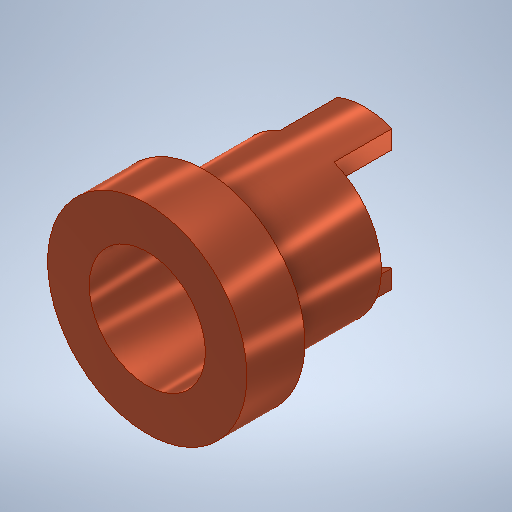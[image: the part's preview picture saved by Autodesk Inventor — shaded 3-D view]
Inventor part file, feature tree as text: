
AUTODESK INVENTOR PART (.ipt)
format: ipt  version: 2025.2 (Build 292293000, 293)  size: 283,648 bytes
history: native  units: mm
features: extrude x4, sketch x4, other x3, projected_geometry x2
ambient origin geometry x8: Origin, YZ Plane, XZ Plane, XY Plane, X Axis, Y Axis, Z Axis, Center Point
bodies: Body1 (feature_tree)
feature tree (13):
  other  "Bryła1"
  extrude  "Wyciągnięcie proste1"  Depth=13.75mm
  extrude  "Wyciągnięcie proste2"  Depth=8.0mm
  other  "Płaszczyzna konstrukcyjna1"
  extrude  "Wyciągnięcie proste3"  Depth=4.0mm TaperAngle=0.0deg
  other  "Płaszczyzna konstrukcyjna2"
  extrude  "Wyciągnięcie proste4"  Depth=10.3mm
  sketch  "Szkic1"
  sketch  "Szkic2"
  sketch  "Szkic3"
  projected_geometry  "Pętla rzutowana1"
  sketch  "Szkic4"
  projected_geometry  "Pętla rzutowana2"
